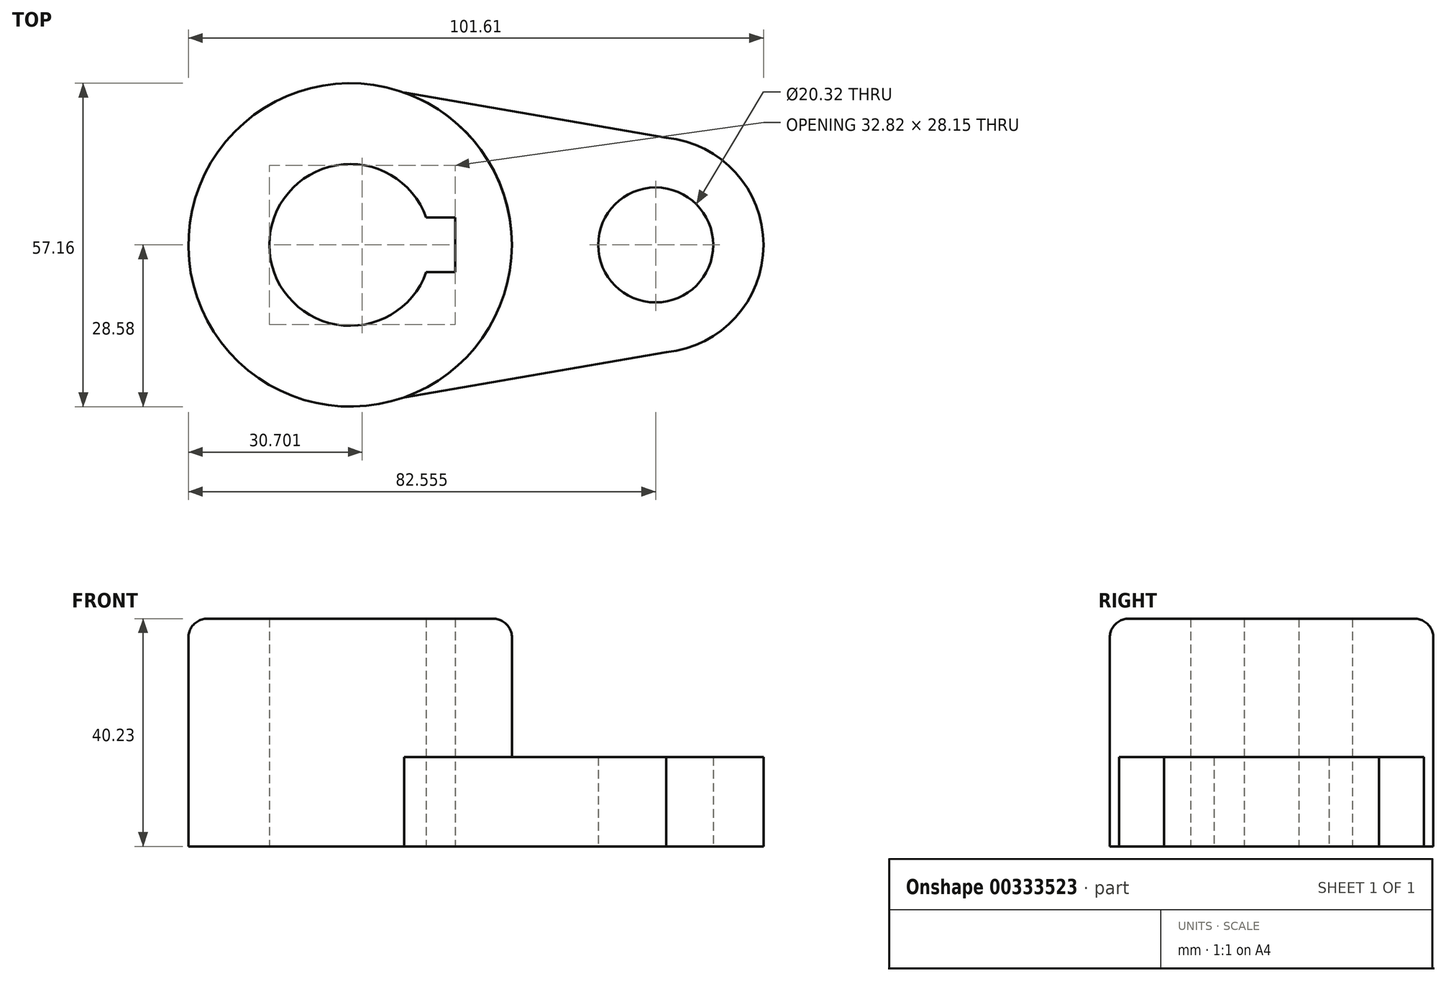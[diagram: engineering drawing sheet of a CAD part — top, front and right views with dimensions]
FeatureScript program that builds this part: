
annotation { "Feature Type Name" : "Feature", "Feature Type Description" : "" }
export const myFeature = defineFeature(function(context is Context, id is Id, definition is map)
    precondition{}
    {
        {
            var Q0;
            Q0=qCreatedBy(makeId("Top.planeOp"),FACE);
            var sketch = newSketch(context, id + "F0", { "sketchPlane" : qUnion([Q0])});
            skCircle(sketch, "E0", {"center": v(0, 0) * mm, "radius": 28.57 * mm});
            skLineSegment(sketch, "E1", {"start": v(0, 28.58) * mm, "end": v(55.83, 18.96) * mm});
            skLineSegment(sketch, "E2.MirrorCS", {"start": v(0, -28.58) * mm, "end": v(55.83, -18.96) * mm});
            skArc(sketch, "E3", {"start": v(55.83, 18.96) * mm, "mid": v(73.03, 0) * mm, "end": v(55.83, -18.96) * mm});
            skCircle(sketch, "E4", {"center": v(53.98, 0) * mm, "radius": 10.16 * mm});
            skArc(sketch, "E5", {"start": v(13.45, 4.83) * mm, "mid": v(-14.29, 0) * mm, "end": v(13.45, -4.83) * mm});
            skLineSegment(sketch, "E6", {"start": v(18.53, 0) * mm, "end": v(18.53, -4.83) * mm});
            skLineSegment(sketch, "E7", {"start": v(18.53, -4.83) * mm, "end": v(13.45, -4.83) * mm});
            skLineSegment(sketch, "E8", {"start": v(18.53, 0) * mm, "end": v(18.53, 4.83) * mm});
            skLineSegment(sketch, "E9", {"start": v(18.53, 4.83) * mm, "end": v(13.45, 4.83) * mm});
            skPoint(sketch, "E10.orphan", {"position": v(-14.29, 0) * mm});
            skSolve(sketch);
        }
        {
            var Q0;
            Q0 = qSketchRegion(id + "F0", true);
            extrude(context, id + "F1", {"entities" : qUnion([Q0]), "depth" : 15.77 * mm, "offsetDistance" : 25.4 * mm});
        }
        {
            var Q0;
            Q0=qCreatedBy(makeId("Top.planeOp"),FACE);
            var sketch = newSketch(context, id + "F2", { "sketchPlane" : qUnion([Q0])});
            skCircle(sketch, "E11", {"center": v(0, 0) * mm, "radius": 28.58 * mm});
            skSolve(sketch);
        }
        {
            var Q0;
            Q0 = qSketchRegion(id + "F2", true);
            extrude(context, id + "F3", {"entities" : qUnion([Q0]), "operationType" : NewBodyOperationType.ADD, "depth" : 40.23 * mm, "offsetDistance" : 25.4 * mm});
        }
        {
            var Q0;
            Q0=qCreatedBy(makeId("Top.planeOp"),FACE);
            var sketch = newSketch(context, id + "F4", { "sketchPlane" : qUnion([Q0])});
            skArc(sketch, "E12", {"start": v(13.45, 4.83) * mm, "mid": v(-14.29, 0) * mm, "end": v(13.45, -4.83) * mm});
            skLineSegment(sketch, "E13", {"start": v(18.53, 0) * mm, "end": v(18.53, 4.83) * mm});
            skLineSegment(sketch, "E14", {"start": v(18.53, 4.83) * mm, "end": v(13.45, 4.83) * mm});
            skLineSegment(sketch, "E15.MirrorCS", {"start": v(18.53, 0) * mm, "end": v(18.53, -4.83) * mm});
            skLineSegment(sketch, "E16.MirrorCS", {"start": v(18.53, -4.83) * mm, "end": v(13.45, -4.83) * mm});
            skPoint(sketch, "E17.orphan", {"position": v(14.29, 0) * mm});
            skSolve(sketch);
        }
        {
            var Q0;
            Q0 = qSketchRegion(id + "F4", true);
            extrude(context, id + "F5", {"entities" : qUnion([Q0]), "operationType" : NewBodyOperationType.REMOVE, "endBound" : BoundingType.THROUGH_ALL, "depth" : 25.4 * mm, "offsetDistance" : 25.4 * mm});
        }
        {
            var Q0;
            Q0=makeQuery(id+"F3.opExtrude","CAP_EDGE",EDGE,{"disambiguationData":[OSD([sQuery(id+"F2.wireOp",EDGE,"E11")])],"isStart":false});
            fillet(context, id + "F6", {"entities" : qUnion([Q0]), "radius" : 3.3 * mm, "tangentPropagation" : true, "allowEdgeOverflow" : false});
        }
    });
